# Revit family: LJT-G
name_source: partatom
category: Lighting Fixtures
units: mm (PartAtom-declared; Revit-internal decimal feet)

## family parameters
Cut with Voids When Loaded = No
Host = Face
Light Source = Yes
OmniClass Number = 23.80.70.11
OmniClass Title = Luminaries for Internal Lighting
Part Type = Normal
Room Calculation Point = No
Round Connector Dimension = Use Diameter
Shared = No

## types (8) — shared parameters
Ceiling Type = Grid
Color Filter = 16777215
Default Elevation = 48"
Description = LED Troffer with Advanced Solid State Technology
Dimming Lamp Color Temperature Shift = Incandescent Lamp Curve
Door = White Flush Steel
Emit Shape Visible in Rendering = No
Finish = Arctic White
Glass = White Glass
Lamp = LED
Load Classification = Lighting
Manufacturer = Columbia Lighting
Model = LJT-G
Power Factor = 1
Shielding = Pattern 12 Acrylic Lens
Tilt Angle = 90.00°
URL = https://www.currentlighting.com
Voltage = 120 V

## per-type parameters (varying)
| type | Apparent Load | Color Temp | Emit from Rectangle Length | Emit from Rectangle Width | Lumen Output | Photometric Web File | Size Option | Wattage Comments | Watts |
| LJT24-50XLG-FSA12-EU | 73 VA | 5000K | 47" | 23" | Extra High Lumen | LJT24-50XLG-FSA12-EU.ies | LJT : 24 | 73W | 73 W |
| LJT24-40XWG-FSA12-EU | 20 VA | 4000K | 47" | 23" | Extra Low Lumen | LJT24-40XWG-FSA12-EU.ies | LJT : 24 | 20W | 20 W |
| LJT22-50VWG-FSA12-EU | 13 VA | 5000K | 23" | 23" | Very High Lumen | LJT22-50VWG-FSA12-EU.ies | LJT : 22 | 13W | 13 W |
| LJT14-30MWG-FSA12-EU | 31 VA | 3000K | 47" | 11" | Medium Low Watts | LJT14-30MWG-FSA12-EU.ies | LJT : 14 | 31W | 31 W |
| LJT24-35MLG-FSA12-EU | 38 VA | 3500K | 47" | 23" | Medium Lumen | LJT24-35MLG-FSA12-EU.ies | LJT : 24 | 34W | 38 W |
| LJT22-30MLG-FSA12-EU | 38 VA | 3000K | 23" | 23" | Medium Lumen | LJT22-30MLG-FSA12-EU.ies | LJT : 22 | 28W | 38 W |
| LJT14-35VLG-FSA12-EU | 59 VA | 3500K | 47" | 11" | Very High Lumen | LJT14-35VLG-FSA12-EU.ies | LJT : 14 | 59W | 59 W |
| LJT14-30HLG-FSA12-EU | 45 VA | 3000K | 47" | 11" | High Lumen | LJT14-30HLG-FSA12-EU.ies | LJT : 14 | 45W | 45 W |

## geometry (parser evidence)
native form markers: Blend x3, Sweep x4
no freeform markers — native parametric forms only
